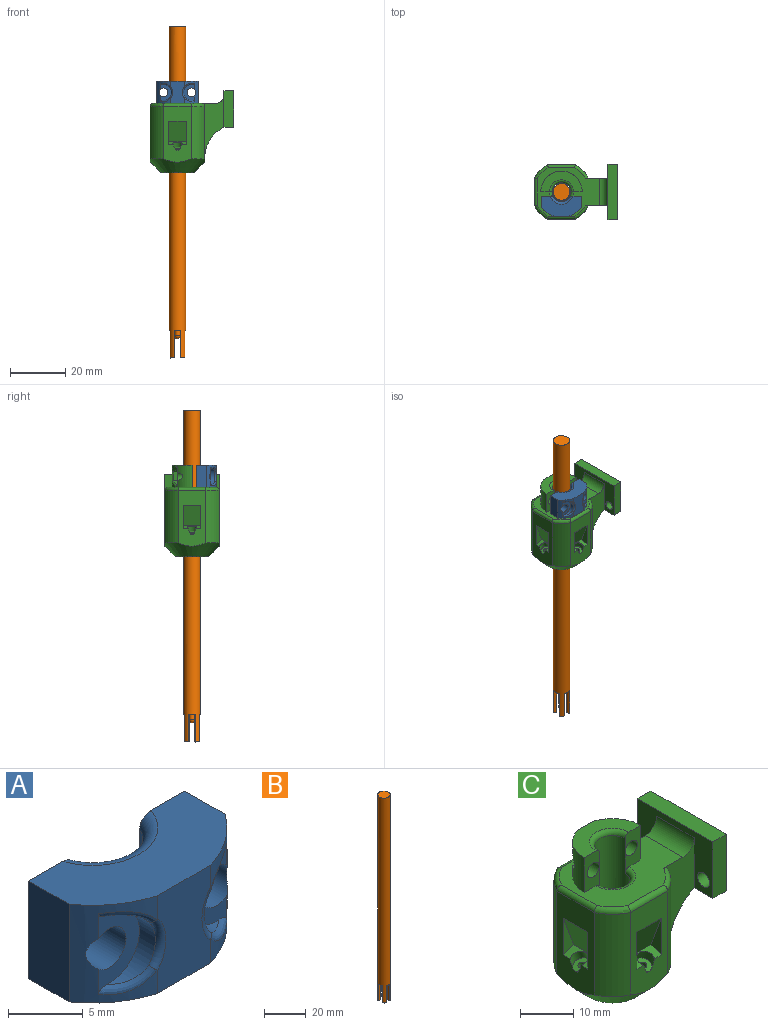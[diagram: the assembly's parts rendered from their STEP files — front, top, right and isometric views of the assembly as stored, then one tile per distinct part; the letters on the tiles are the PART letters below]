
ASSEMBLY  parts=3 mates=2
PART A: 24 faces, bbox 15x7.9x8.3 mm
  f0: plane 8.11x4.4mm, normal (0,1,0), area 25.8mm2, adj f3,f8,f9,f10,f15,f16,f17
  f1: plane 8x5mm, normal (0,-1,0), area 35.2mm2, adj f2,f5,f9,f10,f19,f22
  f2: cylinder r=9mm len=8mm, axis (0,0,-1), area 22.1mm2, adj f1,f3,f8,f9,f10,f14,f21,f22
  f3: cylinder r=1.6mm len=5.28mm, axis (0,1,0), area 53.1mm2, adj f0,f2,f14
  f4: cylinder r=1.6mm len=5.28mm, axis (0,1,0), area 53.1mm2, adj f5,f6,f12
  f5: cylinder r=9mm len=8mm, axis (0,0,-1), area 22.1mm2, adj f1,f4,f7,f9,f10,f12,f18,f19
  f6: plane 8.11x4.4mm, normal (0,1,0), area 25.8mm2, adj f4,f7,f9,f10,f15,f16,f17
  f7: plane 8x3.8mm, normal (-1,0,0), area 30.4mm2, adj f5,f6,f9,f10
  f8: plane 8x3.8mm, normal (1,0,0), area 30.4mm2, adj f0,f2,f9,f10
  f9: plane 14.75x7.28mm, normal (0,0,1), area 76.2mm2, adj f0,f1,f2,f5,f6,f7,f8,f17
  f10: plane 14.75x7.28mm, normal (0,0,-1), area 76.2mm2, adj f0,f1,f2,f5,f6,f7,f8,f16
  f11: cylinder r=2.88mm len=5.75mm, axis (0,-1,0), area 9.9mm2, adj f12,f18,f19,f20
  f12: plane 6.89x4.14mm, normal (0,-1,0), area 11.8mm2, adj f4,f5,f11,f18,f20
  f13: cylinder r=2.88mm len=5.75mm, axis (0,-1,0), area 9.9mm2, adj f14,f21,f22,f23
  f14: plane 6.89x4.14mm, normal (0,-1,0), area 11.8mm2, adj f2,f3,f13,f21,f23
  f15: cylinder r=3.38mm len=6.17mm, axis (0,0,1), area 46.8mm2, adj f0,f6,f16,f17
  f16: torus R=4.38mm, axis (0,0,1), area 14.2mm2, adj f0,f6,f10,f15
  f17: torus R=4.38mm, axis (0,0,1), area 14.2mm2, adj f0,f6,f9,f15
  f18: bspline ~4.68x3.26mm, area 2.7mm2, adj f5,f11,f12,f19
  f19: torus R=3.38mm, axis (0,1,0), area 3.3mm2, adj f1,f5,f11,f18,f20
  f20: bspline ~4.27x2.87mm, area 2.7mm2, adj f5,f11,f12,f19
  f21: bspline ~4.68x3.26mm, area 2.7mm2, adj f2,f13,f14,f22
  f22: torus R=3.38mm, axis (0,1,0), area 3.3mm2, adj f1,f2,f13,f21,f23
  f23: bspline ~4.27x2.87mm, area 2.7mm2, adj f2,f13,f14,f22
PART B: 13 faces, bbox 6x6x120 mm
  f0: plane 1.73x1.68mm, normal (0,0,-1), area 1.8mm2, adj f3,f6
  f1: plane 1.73x1.68mm, normal (0,0,-1), area 1.8mm2, adj f3,f8
  f2: plane 1.73x1.68mm, normal (0,0,-1), area 1.8mm2, adj f3,f7
  f3: cylinder r=3mm len=120mm, axis (0,0,-1), area 2155mm2, adj f0,f1,f2,f4,f5,f6,f7,f8
  f4: plane 6x6mm, normal (0,0,1), area 28.3mm2, adj f3
  f5: plane 1.73x1.68mm, normal (0,0,-1), area 1.8mm2, adj f3,f9
  f6: cylinder r=1mm len=10mm, axis (0,0,-1), area 31.4mm2, adj f0,f3,f10
  f7: cylinder r=1mm len=10mm, axis (0,0,-1), area 31.4mm2, adj f2,f3,f10
  f8: cylinder r=1mm len=10mm, axis (0,0,-1), area 31.4mm2, adj f1,f3,f10
  f9: cylinder r=1mm len=10mm, axis (0,0,-1), area 31.4mm2, adj f3,f5,f10
  f10: plane 6x6mm, normal (0,0,-1), area 17.9mm2, adj f3,f6,f7,f8,f9,f12
  f11: sphere r=1mm, area 6.3mm2, adj f12
  f12: cylinder r=1mm len=2mm, axis (0,0,-1), area 12.6mm2, adj f10,f11
PART C: 80 faces, bbox 36.4x25.4x192.4 mm
  f0: bspline ~19x8.5mm, area 43.1mm2, adj f20,f77
  f1: plane 6.5x2.76mm, normal (-0.35,0,0.94), area 11mm2, adj f4,f72,f73,f76,f78
  f2: bspline ~8.59x4.65mm, area 41.9mm2, adj f20,f74
  f3: plane 6.5x2.76mm, normal (0,0.35,0.94), area 11mm2, adj f7,f67,f68,f69,f75
  f4: plane 23.61x13.41mm, normal (-1,0,0), area 138.2mm2, adj f1,f14,f15,f37,f54,f72,f73,f76
  f5: bspline ~8.59x4.65mm, area 41.9mm2, adj f20,f70
  f6: plane 6.5x2.76mm, normal (0,-0.35,0.94), area 11mm2, adj f8,f64,f65,f66,f71
  f7: plane 23.61x13.41mm, normal (0,1,0), area 138.2mm2, adj f3,f14,f17,f37,f56,f67,f68,f69
  f8: plane 23.61x13.41mm, normal (0,-1,0), area 138.2mm2, adj f6,f15,f16,f37,f52,f64,f65,f66
  f9: plane 23.24x8.38mm, normal (0,-1,0), area 84.8mm2, adj f16,f19,f39,f47,f48,f51
  f10: cylinder r=7.5mm len=8mm, axis (0,0,-1), area 48.5mm2, adj f12,f19,f21,f23,f24,f32,f33,f36
  f11: cylinder r=7.5mm len=8mm, axis (0,0,-1), area 48.5mm2, adj f13,f19,f21,f22,f24,f28,f29,f30
  f12: cylinder r=1.6mm len=5.23mm, axis (0,-1,0), area 47.8mm2, adj f10,f23,f36
  f13: cylinder r=1.6mm len=5.23mm, axis (0,-1,0), area 47.8mm2, adj f11,f22,f30
  f14: cylinder r=11mm len=19mm, axis (0,0,-1), area 131.1mm2, adj f4,f7,f37,f55
  f15: cylinder r=11mm len=19mm, axis (0,0,-1), area 131.1mm2, adj f4,f8,f37,f53
  f16: cylinder r=11mm len=19mm, axis (0,0,-1), area 131.1mm2, adj f8,f9,f37,f51
  f17: cylinder r=11mm len=19mm, axis (0,0,-1), area 131.1mm2, adj f7,f37,f38,f57
  f18: cylinder r=3.38mm len=32mm, axis (0,0,-1), area 593.8mm2, adj f20,f22,f23,f49,f50
  f19: plane 22.6x17.6mm, normal (0,0,1), area 215.6mm2, adj f9,f10,f11,f21,f22,f23,f38,f48
  f20: plane 12.21x12.21mm, normal (0,0,-1), area 72mm2, adj f0,f2,f5,f18,f37
  f21: plane 8.06x4.06mm, normal (0,1,0), area 30.7mm2, adj f10,f11,f19,f24,f58,f59,f60,f61
  f22: plane 9x4.13mm, normal (0,-1,0), area 25mm2, adj f11,f13,f18,f19,f24,f49,f50
  f23: plane 9x4.13mm, normal (0,-1,0), area 25mm2, adj f10,f12,f18,f19,f24,f49,f50
  f24: plane 15x7.23mm, normal (0,0,1), area 57.6mm2, adj f10,f11,f21,f22,f23,f49
  f25: plane 2.43x1.38mm, normal (-0.49,0,-0.87), area 2.1mm2, adj f26,f30,f61
  f26: plane 3.33x1.37mm, normal (-1,0,-0.01), area 4.5mm2, adj f25,f27,f30,f61,f62,f63
  f27: plane 2.46x1.44mm, normal (-0.51,0,0.86), area 2.1mm2, adj f26,f30,f63
  f28: plane 0.88x0.78mm, normal (0.49,0,0.87), area 0.1mm2, adj f11,f30,f63
  f29: plane 0.83x0.74mm, normal (0.51,0,-0.86), area 0.1mm2, adj f11,f30,f61
  f30: plane 6.71x3.2mm, normal (0,1,0), area 11.3mm2, adj f11,f13,f25,f26,f27,f28,f29,f61
  f31: plane 2.43x1.38mm, normal (0.49,0,-0.87), area 2.1mm2, adj f35,f36,f60
  f32: plane 0.83x0.74mm, normal (-0.51,0,-0.86), area 0.1mm2, adj f10,f36,f60
  f33: plane 0.88x0.78mm, normal (-0.49,0,0.87), area 0.1mm2, adj f10,f36,f58
  f34: plane 2.46x1.44mm, normal (0.51,0,0.86), area 2.1mm2, adj f35,f36,f58
  f35: plane 3.33x1.37mm, normal (1,0,-0.01), area 4.5mm2, adj f31,f34,f36,f58,f59,f60
  f36: plane 6.71x3.2mm, normal (0,1,0), area 11.3mm2, adj f10,f12,f31,f32,f33,f34,f35,f58
  f37: cone r=11mm half-angle=45deg, axis (0,0,1), area 369.1mm2, adj f4,f7,f8,f14,f15,f16,f17,f20
  f38: plane 23.24x8.38mm, normal (0,1,0), area 84.8mm2, adj f17,f19,f39,f47,f48,f57
  f39: plane 20x13.05mm, normal (-1,0,0), area 129.7mm2, adj f9,f38,f40,f41,f42,f43,f44,f45
  f40: plane 20x3.5mm, normal (0,0,-1), area 70mm2, adj f39,f41,f44,f46,f47
  f41: plane 13.05x3.5mm, normal (0,1,0), area 45.7mm2, adj f39,f40,f42,f46
  f42: plane 20x3.5mm, normal (0,0,1), area 70mm2, adj f39,f41,f44,f46
  f43: cylinder r=1.6mm len=3.5mm, axis (-1,0,0), area 35.2mm2, adj f39,f46
  f44: plane 13.05x3.5mm, normal (0,-1,0), area 45.7mm2, adj f39,f40,f42,f46
  f45: cylinder r=1.6mm len=3.5mm, axis (-1,0,0), area 35.2mm2, adj f39,f46
  f46: plane 20x13.05mm, normal (1,0,0), area 244.9mm2, adj f40,f41,f42,f43,f44,f45
  f47: cylinder r=12.91mm len=11.48mm, axis (0,-1,0), area 141.4mm2, adj f9,f38,f40,f79
  f48: cylinder r=3mm len=10mm, axis (0,-1,0), area 47.1mm2, adj f9,f19,f38,f39
  f49: torus R=4.38mm, axis (0,0,1), area 18.4mm2, adj f18,f22,f23,f24
  f50: torus R=4.38mm, axis (0,0,1), area 18.4mm2, adj f18,f19,f22,f23
  f51: torus R=10mm, axis (0,0,1), area 9.9mm2, adj f9,f16,f19,f52
  f52: cylinder r=1mm len=10mm, axis (-1,0,0), area 15.3mm2, adj f8,f19,f51,f53
  f53: torus R=10mm, axis (0,0,1), area 10.1mm2, adj f15,f19,f52,f54
  f54: cylinder r=1mm len=10mm, axis (0,1,0), area 15.3mm2, adj f4,f19,f53,f55
  f55: torus R=10mm, axis (0,0,1), area 10.1mm2, adj f14,f19,f54,f56
  f56: cylinder r=1mm len=10mm, axis (1,0,0), area 15.3mm2, adj f7,f19,f55,f57
  f57: torus R=10mm, axis (0,0,1), area 9.9mm2, adj f17,f19,f38,f56
  f58: bspline ~5.01x3.22mm, area 3.6mm2, adj f10,f21,f33,f34,f35,f36,f59
  f59: bspline ~189.02x2.04mm, area 2.7mm2, adj f21,f35,f58,f60
  f60: bspline ~5x3.15mm, area 3.6mm2, adj f10,f21,f31,f32,f35,f36,f59
  f61: bspline ~5x3.15mm, area 3.6mm2, adj f11,f21,f25,f26,f29,f30,f62
  f62: bspline ~189.02x2.04mm, area 2.7mm2, adj f21,f26,f61,f63
  f63: bspline ~5.01x3.22mm, area 3.6mm2, adj f11,f21,f26,f27,f28,f30,f62
  f64: plane 8.51x2.76mm, normal (-1,0,0), area 11.7mm2, adj f6,f8,f66
  f65: plane 8.51x2.76mm, normal (1,0,0), area 11.7mm2, adj f6,f8,f66
  f66: plane 7.49x6.5mm, normal (0,-0.94,-0.35), area 51.9mm2, adj f6,f8,f64,f65
  f67: plane 8.51x2.76mm, normal (1,0,0), area 11.7mm2, adj f3,f7,f69
  f68: plane 8.51x2.76mm, normal (-1,0,0), area 11.7mm2, adj f3,f7,f69
  f69: plane 7.49x6.5mm, normal (0,0.94,-0.35), area 51.9mm2, adj f3,f7,f67,f68
  f70: plane 4.01x3.78mm, normal (0,-0.35,0.94), area 8mm2, adj f5,f8,f71
  f71: cylinder r=1.75mm len=3.95mm, axis (0,-0.35,0.94), area 18mm2, adj f6,f8,f70
  f72: plane 8.51x2.76mm, normal (0,1,0), area 11.7mm2, adj f1,f4,f76
  f73: plane 8.51x2.76mm, normal (0,-1,0), area 11.7mm2, adj f1,f4,f76
  f74: plane 4.01x3.78mm, normal (0,0.35,0.94), area 8mm2, adj f2,f7,f75
  f75: cylinder r=1.75mm len=3.95mm, axis (0,0.35,0.94), area 18mm2, adj f3,f7,f74
  f76: plane 7.49x6.5mm, normal (-0.94,0,-0.35), area 51.9mm2, adj f1,f4,f72,f73
  f77: plane 4.54x4.3mm, normal (-0.35,0,0.94), area 8mm2, adj f0,f4,f78
  f78: cylinder r=1.75mm len=3.95mm, axis (-0.35,0,0.94), area 18mm2, adj f1,f4,f77
  f79: plane 10.87x2.07mm, normal (1,0,0), area 7.9mm2, adj f37,f47
PLACE A t=(53.04,6.37,31.74)mm
PLACE B t=(3.04,6.5,-60.26)mm
PLACE C t=(3.04,6.5,6.74)mm
MATE fastened B.f3 <-> C.f18  axis (0,0,1) through (3.04,6.5,59.74)mm
MATE fastened A.f3 <-> C.f12  axis (0,1,0) through (8.11,5,35.74)mm
